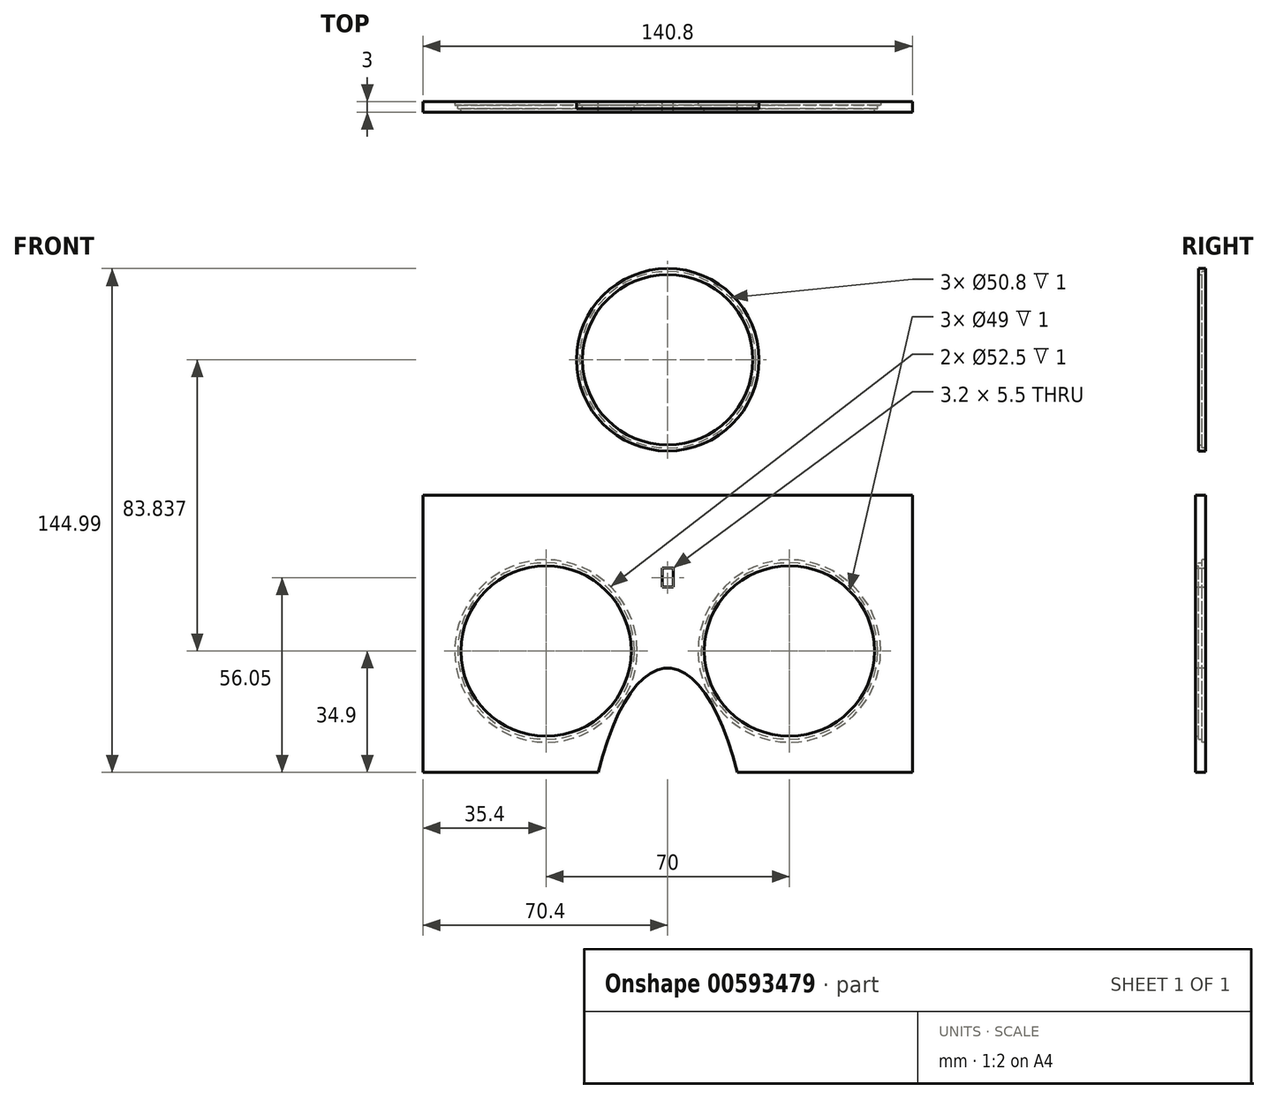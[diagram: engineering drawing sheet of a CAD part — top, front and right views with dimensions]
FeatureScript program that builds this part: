
annotation { "Feature Type Name" : "Feature", "Feature Type Description" : "" }
export const myFeature = defineFeature(function(context is Context, id is Id, definition is map)
    precondition{}
    {
        {
            var Q0;
            Q0=qCreatedBy(makeId("Front.planeOp"),FACE);
            var sketch = newSketch(context, id + "F0", { "sketchPlane" : qUnion([Q0])});
            skLineSegment(sketch, "E0.bottom", {"start": v(70.4, 39.9) * mm, "end": v(-70.4, 39.9) * mm});
            skLineSegment(sketch, "E0.top", {"start": v(70.4, -39.9) * mm, "end": v(-70.4, -39.9) * mm});
            skLineSegment(sketch, "E0.left", {"start": v(70.4, 39.9) * mm, "end": v(70.4, -39.9) * mm});
            skLineSegment(sketch, "E0.right", {"start": v(-70.4, 39.9) * mm, "end": v(-70.4, -39.9) * mm});
            skPoint(sketch, "E0.middle", {"position": v(0, 0) * mm});
            skLineSegment(sketch, "E1.bottom", {"start": v(-54.7, 39.9) * mm, "end": v(-39.9, 39.9) * mm});
            skLineSegment(sketch, "E1.top", {"start": v(-54.7, 42.9) * mm, "end": v(-39.9, 42.9) * mm});
            skLineSegment(sketch, "E1.left", {"start": v(-54.7, 39.9) * mm, "end": v(-54.7, 42.9) * mm});
            skLineSegment(sketch, "E1.right", {"start": v(-39.9, 39.9) * mm, "end": v(-39.9, 42.9) * mm});
            skLineSegment(sketch, "E2.bottom", {"start": v(54.7, 39.9) * mm, "end": v(39.9, 39.9) * mm});
            skLineSegment(sketch, "E2.top", {"start": v(54.7, 42.9) * mm, "end": v(39.9, 42.9) * mm});
            skLineSegment(sketch, "E2.left", {"start": v(54.7, 39.9) * mm, "end": v(54.7, 42.9) * mm});
            skLineSegment(sketch, "E2.right", {"start": v(39.9, 39.9) * mm, "end": v(39.9, 42.9) * mm});
            skLineSegment(sketch, "E3.bottom", {"start": v(39.9, -39.9) * mm, "end": v(54.7, -39.9) * mm});
            skLineSegment(sketch, "E3.top", {"start": v(39.9, -42.9) * mm, "end": v(54.7, -42.9) * mm});
            skLineSegment(sketch, "E3.left", {"start": v(39.9, -39.9) * mm, "end": v(39.9, -42.9) * mm});
            skLineSegment(sketch, "E3.right", {"start": v(54.7, -39.9) * mm, "end": v(54.7, -42.9) * mm});
            skLineSegment(sketch, "E4.bottom", {"start": v(-54.7, -39.9) * mm, "end": v(-39.9, -39.9) * mm});
            skLineSegment(sketch, "E4.top", {"start": v(-54.7, -42.9) * mm, "end": v(-39.9, -42.9) * mm});
            skLineSegment(sketch, "E4.left", {"start": v(-54.7, -39.9) * mm, "end": v(-54.7, -42.9) * mm});
            skLineSegment(sketch, "E4.right", {"start": v(-39.9, -39.9) * mm, "end": v(-39.9, -42.9) * mm});
            skCircle(sketch, "E5", {"center": v(-35, -5) * mm, "radius": 25.4 * mm});
            skCircle(sketch, "E6", {"center": v(35, -5) * mm, "radius": 25.4 * mm});
            skEllipse(sketch, "E7", {"center": v(0, -84.9) * mm, "majorRadius": 75 * mm, "minorRadius": 25 * mm, "majorAxis": v(0, 1)});
            skCircle(sketch, "E8", {"center": v(-35, -5) * mm, "radius": 24.5 * mm});
            skCircle(sketch, "E9", {"center": v(35, -5) * mm, "radius": 24.5 * mm});
            skLineSegment(sketch, "E10.bottom", {"start": v(1.6, 13.4) * mm, "end": v(-1.6, 13.4) * mm});
            skLineSegment(sketch, "E10.top", {"start": v(1.6, 18.9) * mm, "end": v(-1.6, 18.9) * mm});
            skLineSegment(sketch, "E10.left", {"start": v(1.6, 13.4) * mm, "end": v(1.6, 18.9) * mm});
            skLineSegment(sketch, "E10.right", {"start": v(-1.6, 13.4) * mm, "end": v(-1.6, 18.9) * mm});
            skPoint(sketch, "E10.middle", {"position": v(0, 16.15) * mm});
            skCircle(sketch, "E11", {"center": v(-35, -5) * mm, "radius": 26.25 * mm});
            skCircle(sketch, "E12", {"center": v(35, -5) * mm, "radius": 26.25 * mm});
            skSolve(sketch);
        }
        {
            var Q0;
            Q0=qCreatedBy(makeId("Front.planeOp"),FACE);
            var sketch = newSketch(context, id + "F1", { "sketchPlane" : qUnion([Q0])});
            skCircle(sketch, "E13", {"center": v(0, 78.84) * mm, "radius": 24.5 * mm});
            skCircle(sketch, "E14", {"center": v(0, 78.84) * mm, "radius": 26.25 * mm});
            skCircle(sketch, "E15", {"center": v(0, 78.84) * mm, "radius": 25.4 * mm});
            skSolve(sketch);
        }
        {
            var Q0;
            {var subQ2=sQuery(id+"F0.wireOp",EDGE,"E0.left");Q0=makeQuery(id+"F0.imprint","IMPRINT",FACE,{"disambiguationData":[TD([[makeQuery(id+"F0.imprint","IMPRINT",EDGE,{"derivedFrom":subQ2}),-1.0]])]});}
            var Q1;
            Q1=makeQuery(id+"F0.imprint","IMPRINT",FACE,{"disambiguationData":[TD([[makeQuery(id+"F0.imprint","IMPRINT",EDGE,{"derivedFrom":sQuery(id+"F0.wireOp",EDGE,"E1.bottom")}),1.0]])]});
            var Q2;
            Q2=makeQuery(id+"F0.imprint","IMPRINT",FACE,{"disambiguationData":[TD([[makeQuery(id+"F0.imprint","IMPRINT",EDGE,{"derivedFrom":sQuery(id+"F0.wireOp",EDGE,"E4.bottom")}),-1.0]])]});
            var Q3;
            Q3=makeQuery(id+"F0.imprint","IMPRINT",FACE,{"disambiguationData":[TD([[makeQuery(id+"F0.imprint","IMPRINT",EDGE,{"derivedFrom":sQuery(id+"F0.wireOp",EDGE,"E3.bottom")}),-1.0]])]});
            var Q4;
            Q4=makeQuery(id+"F0.imprint","IMPRINT",FACE,{"disambiguationData":[TD([[makeQuery(id+"F0.imprint","IMPRINT",EDGE,{"derivedFrom":sQuery(id+"F0.wireOp",EDGE,"E2.bottom")}),-1.0]])]});
            var Q5;
            Q5=makeQuery(id+"F0.imprint","IMPRINT",FACE,{"disambiguationData":[TD([[makeQuery(id+"F0.imprint","IMPRINT",EDGE,{"derivedFrom":sQuery(id+"F0.wireOp",EDGE,"E5")}),-1.0]])]});
            var Q6;
            Q6=makeQuery(id+"F0.imprint","IMPRINT",FACE,{"disambiguationData":[TD([[makeQuery(id+"F0.imprint","IMPRINT",EDGE,{"derivedFrom":sQuery(id+"F0.wireOp",EDGE,"E6")}),-1.0]])]});
            extrude(context, id + "F2", {"entities" : qUnion([Q0, Q1, Q2, Q3, Q4, Q5, Q6]), "depth" : 2 * mm, "offsetDistance" : 25 * mm, "hasSecondDirection" : true, "secondDirectionOppositeDirection" : true, "secondDirectionDepth" : 1 * mm});
        }
        {
            var Q0;
            Q0=makeQuery(id+"F0.imprint","IMPRINT",FACE,{"disambiguationData":[TD([[makeQuery(id+"F0.imprint","IMPRINT",EDGE,{"derivedFrom":sQuery(id+"F0.wireOp",EDGE,"E6")}),-1.0]])]});
            var Q1;
            Q1=makeQuery(id+"F0.imprint","IMPRINT",FACE,{"disambiguationData":[TD([[makeQuery(id+"F0.imprint","IMPRINT",EDGE,{"derivedFrom":sQuery(id+"F0.wireOp",EDGE,"E5")}),-1.0]])]});
            var Q2;
            Q2=makeQuery(id+"F2.opExtrude","CAP_FACE",FACE,{"disambiguationData":[OSD([sQuery(id+"F0.wireOp",EDGE,"E0.bottom"),sQuery(id+"F0.wireOp",EDGE,"E0.top"),sQuery(id+"F0.wireOp",EDGE,"E0.left"),sQuery(id+"F0.wireOp",EDGE,"E0.right"),sQuery(id+"F0.wireOp",EDGE,"E1.top"),sQuery(id+"F0.wireOp",EDGE,"E1.left"),sQuery(id+"F0.wireOp",EDGE,"E1.right"),sQuery(id+"F0.wireOp",EDGE,"E2.top"),sQuery(id+"F0.wireOp",EDGE,"E2.left"),sQuery(id+"F0.wireOp",EDGE,"E2.right"),sQuery(id+"F0.wireOp",EDGE,"E3.top"),sQuery(id+"F0.wireOp",EDGE,"E3.left"),sQuery(id+"F0.wireOp",EDGE,"E3.right"),sQuery(id+"F0.wireOp",EDGE,"E4.top"),sQuery(id+"F0.wireOp",EDGE,"E4.left"),sQuery(id+"F0.wireOp",EDGE,"E4.right"),sQuery(id+"F0.wireOp",EDGE,"E5"),sQuery(id+"F0.wireOp",EDGE,"E6"),sQuery(id+"F0.wireOp",EDGE,"E7"),sQuery(id+"F0.wireOp",EDGE,"E10.bottom"),sQuery(id+"F0.wireOp",EDGE,"E10.top"),sQuery(id+"F0.wireOp",EDGE,"E10.left"),sQuery(id+"F0.wireOp",EDGE,"E10.right")])],"isStart":true});
            extrude(context, id + "F3", {"entities" : qUnion([Q0, Q1]), "operationType" : NewBodyOperationType.REMOVE, "endBound" : BoundingType.UP_TO_SURFACE, "oppositeDirection" : true, "depth" : 25 * mm, "endBoundEntityFace" : qUnion([Q2]), "offsetDistance" : 2 * mm, "offsetOppositeDirection" : true});
        }
        {
            var Q0;
            Q0=makeQuery(id+"F0.imprint","IMPRINT",FACE,{"disambiguationData":[TD([[makeQuery(id+"F0.imprint","IMPRINT",EDGE,{"derivedFrom":sQuery(id+"F0.wireOp",EDGE,"E6")}),1.0]])]});
            var Q1;
            Q1=makeQuery(id+"F0.imprint","IMPRINT",FACE,{"disambiguationData":[TD([[makeQuery(id+"F0.imprint","IMPRINT",EDGE,{"derivedFrom":sQuery(id+"F0.wireOp",EDGE,"E5")}),1.0]])]});
            var Q2;
            Q2=makeQuery(id+"F2.opExtrude","CAP_FACE",FACE,{"disambiguationData":[OSD([sQuery(id+"F0.wireOp",EDGE,"E0.bottom"),sQuery(id+"F0.wireOp",EDGE,"E0.top"),sQuery(id+"F0.wireOp",EDGE,"E0.left"),sQuery(id+"F0.wireOp",EDGE,"E0.right"),sQuery(id+"F0.wireOp",EDGE,"E1.top"),sQuery(id+"F0.wireOp",EDGE,"E1.left"),sQuery(id+"F0.wireOp",EDGE,"E1.right"),sQuery(id+"F0.wireOp",EDGE,"E2.top"),sQuery(id+"F0.wireOp",EDGE,"E2.left"),sQuery(id+"F0.wireOp",EDGE,"E2.right"),sQuery(id+"F0.wireOp",EDGE,"E3.top"),sQuery(id+"F0.wireOp",EDGE,"E3.left"),sQuery(id+"F0.wireOp",EDGE,"E3.right"),sQuery(id+"F0.wireOp",EDGE,"E4.top"),sQuery(id+"F0.wireOp",EDGE,"E4.left"),sQuery(id+"F0.wireOp",EDGE,"E4.right"),sQuery(id+"F0.wireOp",EDGE,"E5"),sQuery(id+"F0.wireOp",EDGE,"E6"),sQuery(id+"F0.wireOp",EDGE,"E7"),sQuery(id+"F0.wireOp",EDGE,"E10.bottom"),sQuery(id+"F0.wireOp",EDGE,"E10.top"),sQuery(id+"F0.wireOp",EDGE,"E10.left"),sQuery(id+"F0.wireOp",EDGE,"E10.right")])],"isStart":false});
            extrude(context, id + "F4", {"entities" : qUnion([Q0, Q1]), "operationType" : NewBodyOperationType.ADD, "depth" : 2 * mm, "endBoundEntityFace" : qUnion([Q2]), "hasOffset" : true, "offsetDistance" : 2 * mm, "offsetOppositeDirection" : true, "hasSecondDirection" : true, "secondDirectionOppositeDirection" : false, "secondDirectionDepth" : 1 * mm});
        }
        {
            var Q0;
            Q0=makeQuery(id+"F1.imprint","IMPRINT",FACE,{"disambiguationData":[TD([[makeQuery(id+"F1.imprint","IMPRINT",EDGE,{"derivedFrom":sQuery(id+"F1.wireOp",EDGE,"E14")}),1.0]])]});
            extrude(context, id + "F5", {"entities" : qUnion([Q0]), "oppositeDirection" : true, "depth" : 1 * mm, "offsetDistance" : 25 * mm});
        }
        {
            var Q0;
            Q0=makeQuery(id+"F1.imprint","IMPRINT",FACE,{"disambiguationData":[TD([[makeQuery(id+"F1.imprint","IMPRINT",EDGE,{"derivedFrom":sQuery(id+"F1.wireOp",EDGE,"E13")}),-1.0]])]});
            var Q1;
            Q1=makeQuery(id+"F1.imprint","IMPRINT",FACE,{"disambiguationData":[TD([[makeQuery(id+"F1.imprint","IMPRINT",EDGE,{"derivedFrom":sQuery(id+"F1.wireOp",EDGE,"E14")}),1.0]])]});
            extrude(context, id + "F6", {"entities" : qUnion([Q0, Q1]), "operationType" : NewBodyOperationType.ADD, "depth" : 1 * mm, "offsetDistance" : 25 * mm});
        }
    });
